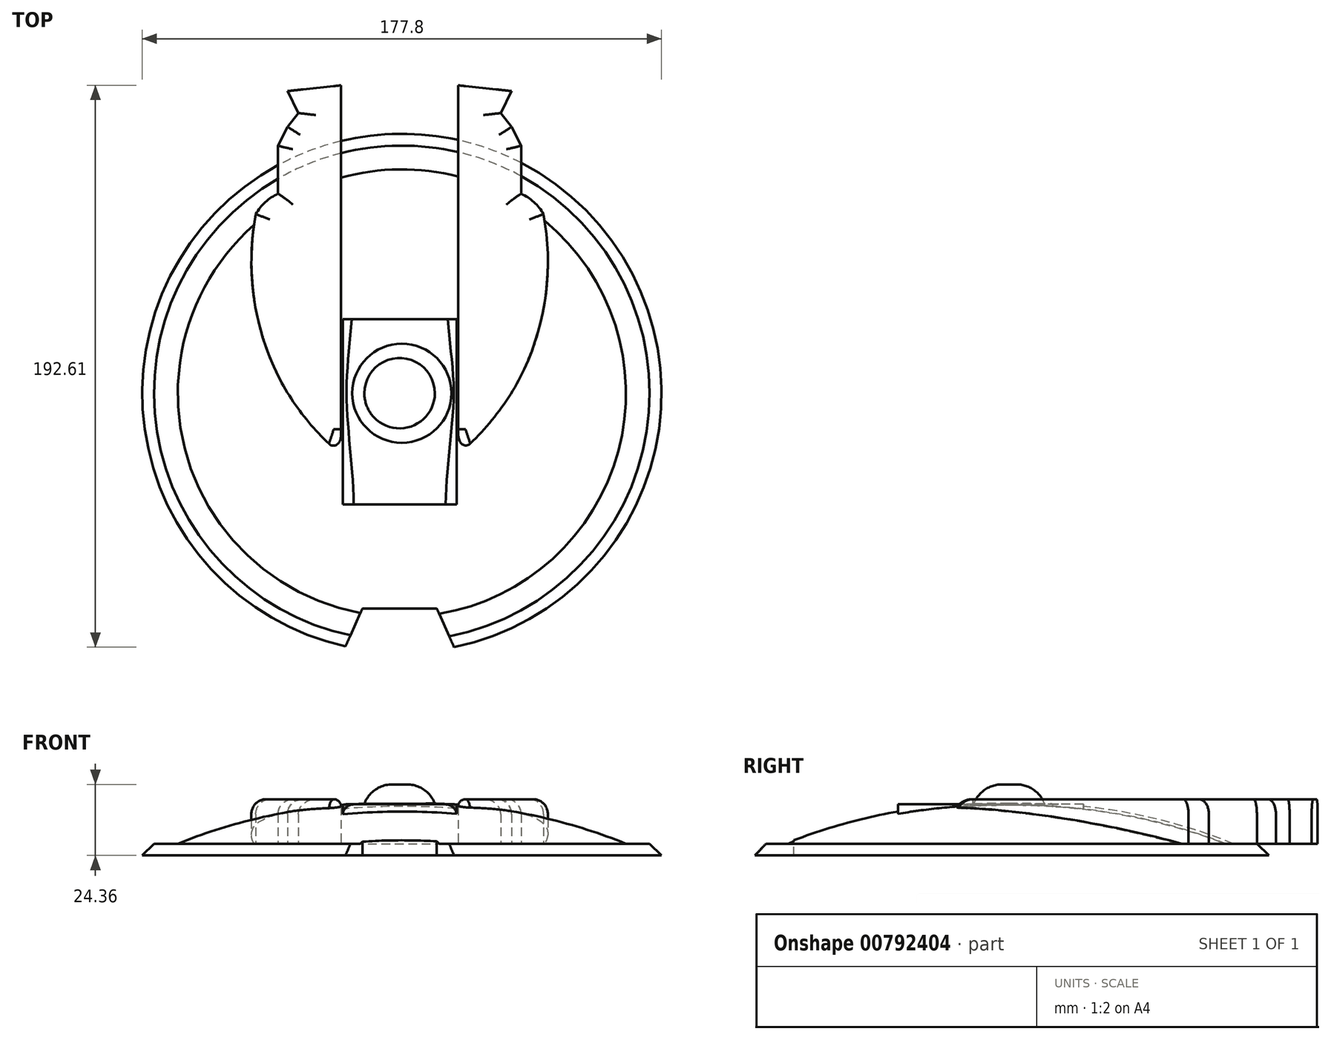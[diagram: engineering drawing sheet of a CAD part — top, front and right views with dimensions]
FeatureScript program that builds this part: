
annotation { "Feature Type Name" : "Feature", "Feature Type Description" : "" }
export const myFeature = defineFeature(function(context is Context, id is Id, definition is map)
    precondition{}
    {
        {
            var Q0;
            Q0=qCreatedBy(makeId("Front.planeOp"),FACE);
            var sketch = newSketch(context, id + "F0", { "sketchPlane" : qUnion([Q0])});
            skArc(sketch, "E0", {"start": v(0.77, 13.74) * mm, "mid": v(-38.3, 10.84) * mm, "end": v(-75.95, 0) * mm});
            skLineSegment(sketch, "E1", {"start": v(-75.95, 0) * mm, "end": v(-84.09, 0) * mm});
            skLineSegment(sketch, "E2", {"start": v(-84.09, 0) * mm, "end": v(-88.13, -4.04) * mm});
            skLineSegment(sketch, "E3", {"start": v(-88.13, -4.04) * mm, "end": v(0.77, -4.04) * mm});
            skLineSegment(sketch, "E4", {"start": v(0.77, -4.04) * mm, "end": v(0.77, 13.74) * mm});
            skSolve(sketch);
        }
        {
            var Q0;
            Q0 = qSketchRegion(id + "F0", true);
            var Q1;
            Q1=sQuery(id+"F0.wireOp",EDGE,"E4");
            revolve(context, id + "F1", {"surfaceOperationType" : NewSurfaceOperationType.NEW, "entities" : qUnion([Q0]), "axis" : qUnion([Q1]), "revolveType" : RevolveType.FULL});
        }
        {
            var Q0;
            Q0=qCreatedBy(makeId("Top.planeOp"),FACE);
            var sketch = newSketch(context, id + "F2", { "sketchPlane" : qUnion([Q0])});
            skCircle(sketch, "E5", {"center": v(0, 0) * mm, "radius": 12.7 * mm});
            skSolve(sketch);
        }
        {
            var Q0;
            Q0 = qSketchRegion(id + "F2", true);
            extrude(context, id + "F3", {"entities" : qUnion([Q0]), "depth" : 20.32 * mm, "offsetDistance" : 25.4 * mm});
        }
        {
            var Q0;
            Q0=makeQuery(id+"F3.opExtrude","CAP_EDGE",EDGE,{"disambiguationData":[OSD([sQuery(id+"F2.wireOp",EDGE,"E5")])],"isStart":false});
            fillet(context, id + "F4", {"entities" : qUnion([Q0]), "radius" : 10.16 * mm, "tangentPropagation" : true, "defaultsChanged" : false, "vertexSettings" : [], "allowEdgeOverflow" : false});
        }
        {
            var Q0;
            Q0=qCreatedBy(makeId("Front.planeOp"),FACE);
            var sketch = newSketch(context, id + "F5", { "sketchPlane" : qUnion([Q0])});
            skLineSegment(sketch, "E6.bottom", {"start": v(19.5, 3.7) * mm, "end": v(-19.5, 3.7) * mm});
            skLineSegment(sketch, "E6.top", {"start": v(19.5, 13.47) * mm, "end": v(-19.5, 13.47) * mm});
            skLineSegment(sketch, "E6.left", {"start": v(19.5, 3.7) * mm, "end": v(19.5, 13.47) * mm});
            skLineSegment(sketch, "E6.right", {"start": v(-19.5, 3.7) * mm, "end": v(-19.5, 13.47) * mm});
            skPoint(sketch, "E6.middle", {"position": v(0, 8.59) * mm});
            skSolve(sketch);
        }
        {
            var Q0;
            Q0 = qSketchRegion(id + "F5", true);
            extrude(context, id + "F6", {"entities" : qUnion([Q0]), "operationType" : NewBodyOperationType.ADD, "depth" : 38.1 * mm, "offsetDistance" : 25.4 * mm});
        }
        {
            var Q0;
            Q0 = qSketchRegion(id + "F5", true);
            extrude(context, id + "F7", {"entities" : qUnion([Q0]), "operationType" : NewBodyOperationType.ADD, "oppositeDirection" : true, "depth" : 25.4 * mm, "offsetDistance" : 25.4 * mm});
        }
        {
            var Q0;
            Q0=makeQuery(id+"F6.opExtrude","SWEPT_EDGE",EDGE,{"disambiguationData":[OSD([sQuery(id+"F5.wireOp",EDGE,"E6.top"),sQuery(id+"F5.wireOp",EDGE,"E6.left")])]});
            var Q1;
            Q1=makeQuery(id+"F6.opExtrude","SWEPT_EDGE",EDGE,{"disambiguationData":[OSD([sQuery(id+"F5.wireOp",EDGE,"E6.top"),sQuery(id+"F5.wireOp",EDGE,"E6.right")])]});
            fillet(context, id + "F8", {"entities" : qUnion([Q0, Q1]), "radius" : 3.8 * mm, "tangentPropagation" : true, "allowEdgeOverflow" : false});
        }
        {
            var Q0;
            Q0=qCreatedBy(makeId("Top.planeOp"),FACE);
            var sketch = newSketch(context, id + "F9", { "sketchPlane" : qUnion([Q0])});
            skLineSegment(sketch, "E7", {"start": v(-20.02, -21.77) * mm, "end": v(-20.02, 105.53) * mm});
            skArc(sketch, "E8", {"start": v(-49.26, 61.37) * mm, "mid": v(-45.77, 15.89) * mm, "end": v(-20.02, -21.77) * mm});
            skArc(sketch, "E9", {"start": v(-41.62, 68.38) * mm, "mid": v(-46, 65.49) * mm, "end": v(-49.26, 61.37) * mm});
            skLineSegment(sketch, "E10", {"start": v(-41.62, 68.38) * mm, "end": v(-41.62, 84.81) * mm});
            skLineSegment(sketch, "E11", {"start": v(-41.62, 84.81) * mm, "end": v(-38.35, 91.3) * mm});
            skLineSegment(sketch, "E12", {"start": v(-38.35, 91.3) * mm, "end": v(-34.66, 96) * mm});
            skLineSegment(sketch, "E13", {"start": v(-34.66, 96) * mm, "end": v(-38.35, 103.56) * mm});
            skLineSegment(sketch, "E14", {"start": v(-38.35, 103.56) * mm, "end": v(-20.02, 105.53) * mm});
            skLineSegment(sketch, "E15.MirrorCS", {"start": v(38.35, 103.56) * mm, "end": v(20.02, 105.53) * mm});
            skLineSegment(sketch, "E16.MirrorCS", {"start": v(20.02, -21.77) * mm, "end": v(20.02, 105.53) * mm});
            skLineSegment(sketch, "E17.MirrorCS", {"start": v(34.66, 96) * mm, "end": v(38.35, 103.56) * mm});
            skLineSegment(sketch, "E18.MirrorCS", {"start": v(38.35, 91.3) * mm, "end": v(34.66, 96) * mm});
            skLineSegment(sketch, "E19.MirrorCS", {"start": v(41.62, 84.81) * mm, "end": v(38.35, 91.3) * mm});
            skLineSegment(sketch, "E20.MirrorCS", {"start": v(41.62, 68.38) * mm, "end": v(41.62, 84.81) * mm});
            skArc(sketch, "E21.MirrorCS", {"start": v(41.62, 68.38) * mm, "mid": v(46, 65.49) * mm, "end": v(49.26, 61.37) * mm});
            skArc(sketch, "E22.MirrorCS", {"start": v(49.26, 61.37) * mm, "mid": v(45.77, 15.89) * mm, "end": v(20.02, -21.77) * mm});
            skSolve(sketch);
        }
        {
            var Q0;
            Q0 = qSketchRegion(id + "F9", true);
            extrude(context, id + "F10", {"entities" : qUnion([Q0]), "operationType" : NewBodyOperationType.ADD, "depth" : 15.24 * mm, "offsetDistance" : 25.4 * mm});
        }
        {
            var Q0;
            Q0=makeQuery(id+"F10.opExtrude","CAP_EDGE",EDGE,{"disambiguationData":[OSD([sQuery(id+"F9.wireOp",EDGE,"E22.MirrorCS")])],"isStart":false});
            var Q1;
            Q1=makeQuery(id+"F10.opExtrude","CAP_EDGE",EDGE,{"disambiguationData":[OSD([sQuery(id+"F9.wireOp",EDGE,"E20.MirrorCS")])],"isStart":false});
            var Q2;
            Q2=makeQuery(id+"F10.opExtrude","CAP_EDGE",EDGE,{"disambiguationData":[OSD([sQuery(id+"F9.wireOp",EDGE,"E21.MirrorCS")])],"isStart":false});
            var Q3;
            Q3=makeQuery(id+"F10.opExtrude","CAP_EDGE",EDGE,{"disambiguationData":[OSD([sQuery(id+"F9.wireOp",EDGE,"E19.MirrorCS")])],"isStart":false});
            var Q4;
            Q4=makeQuery(id+"F10.opExtrude","CAP_EDGE",EDGE,{"disambiguationData":[OSD([sQuery(id+"F9.wireOp",EDGE,"E18.MirrorCS")])],"isStart":false});
            var Q5;
            Q5=makeQuery(id+"F10.opExtrude","CAP_EDGE",EDGE,{"disambiguationData":[OSD([sQuery(id+"F9.wireOp",EDGE,"E17.MirrorCS")])],"isStart":false});
            var Q6;
            Q6=makeQuery(id+"F10.opExtrude","CAP_EDGE",EDGE,{"disambiguationData":[OSD([sQuery(id+"F9.wireOp",EDGE,"E8")])],"isStart":false});
            var Q7;
            Q7=makeQuery(id+"F10.opExtrude","CAP_EDGE",EDGE,{"disambiguationData":[OSD([sQuery(id+"F9.wireOp",EDGE,"E10")])],"isStart":false});
            var Q8;
            Q8=makeQuery(id+"F10.opExtrude","CAP_EDGE",EDGE,{"disambiguationData":[OSD([sQuery(id+"F9.wireOp",EDGE,"E9")])],"isStart":false});
            var Q9;
            Q9=makeQuery(id+"F10.opExtrude","CAP_EDGE",EDGE,{"disambiguationData":[OSD([sQuery(id+"F9.wireOp",EDGE,"E12")])],"isStart":false});
            var Q10;
            Q10=makeQuery(id+"F10.opExtrude","CAP_EDGE",EDGE,{"disambiguationData":[OSD([sQuery(id+"F9.wireOp",EDGE,"E11")])],"isStart":false});
            var Q11;
            Q11=makeQuery(id+"F10.opExtrude","CAP_EDGE",EDGE,{"disambiguationData":[OSD([sQuery(id+"F9.wireOp",EDGE,"E13")])],"isStart":false});
            fillet(context, id + "F11", {"entities" : qUnion([Q0, Q1, Q2, Q3, Q4, Q5, Q6, Q7, Q8, Q9, Q10, Q11]), "tangentPropagation" : true, "radius" : 5.08 * mm, "defaultsChanged" : false, "vertexSettings" : [], "allowEdgeOverflow" : false});
        }
        {
            var Q0;
            Q0=makeQuery(id+"F10.opExtrude","CAP_EDGE",EDGE,{"disambiguationData":[OSD([sQuery(id+"F9.wireOp",EDGE,"E16.MirrorCS")])],"isStart":false});
            var Q1;
            Q1=makeQuery(id+"F10.opExtrude","CAP_EDGE",EDGE,{"disambiguationData":[OSD([sQuery(id+"F9.wireOp",EDGE,"E7")])],"isStart":false});
            fillet(context, id + "F12", {"entities" : qUnion([Q0, Q1]), "tangentPropagation" : true, "radius" : 2.54 * mm, "defaultsChanged" : false, "vertexSettings" : [], "allowEdgeOverflow" : false});
        }
        {
            var Q0;
            Q0=qCreatedBy(makeId("Top.planeOp"),FACE);
            var sketch = newSketch(context, id + "F13", { "sketchPlane" : qUnion([Q0])});
            skLineSegment(sketch, "E23", {"start": v(-12.73, -73.8) * mm, "end": v(-18.96, -87.77) * mm});
            skLineSegment(sketch, "E24", {"start": v(-12.73, -73.8) * mm, "end": v(0, -73.8) * mm});
            skLineSegment(sketch, "E25", {"start": v(0, -73.8) * mm, "end": v(0, -93) * mm});
            skLineSegment(sketch, "E26", {"start": v(0, -93) * mm, "end": v(-18.96, -87.77) * mm});
            skLineSegment(sketch, "E27.MirrorCS", {"start": v(12.73, -73.8) * mm, "end": v(0, -73.8) * mm});
            skLineSegment(sketch, "E28.MirrorCS", {"start": v(12.73, -73.8) * mm, "end": v(18.96, -87.77) * mm});
            skLineSegment(sketch, "E29.MirrorCS", {"start": v(0, -93) * mm, "end": v(18.96, -87.77) * mm});
            skSolve(sketch);
        }
        {
            var Q0;
            Q0 = qSketchRegion(id + "F13", true);
            extrude(context, id + "F14", {"entities" : qUnion([Q0]), "operationType" : NewBodyOperationType.REMOVE, "endBound" : BoundingType.SYMMETRIC, "oppositeDirection" : true, "depth" : 25.4 * mm, "offsetDistance" : 25.4 * mm});
        }
    });
